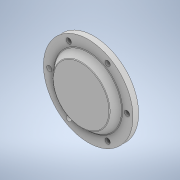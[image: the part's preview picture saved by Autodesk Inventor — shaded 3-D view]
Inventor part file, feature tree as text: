
AUTODESK INVENTOR PART (.ipt)
format: ipt  version: 2020 (Build 240168000, 168)  size: 181,248 bytes
history: native  units: mm
features: sketch x5, reference x4, extrude x3, projected_geometry x3, other x3, plane x2, loft x1, fillet x1
ambient origin geometry x8: Origin, YZ Plane, XZ Plane, XY Plane, X Axis, Y Axis, Z Axis, Center Point
bodies: 实体1 (feature_tree)
feature tree (22):
  plane  "工作平面1"
  extrude  "拉伸1"  Depth=11.0mm
  extrude  "拉伸2"  Depth=12.0mm TaperAngle=0.0deg
  sketch  "草图3"  dims[d8=10.0mm d9=10.5mm d10=0.0mm]
  plane  "工作平面2"
  loft  "放样1"
  extrude  "拉伸3"  Depth=15.0mm
  fillet  "圆角1"  [1 undecoded]
  sketch  "草图1"  dims[d0=165.0mm d1=11.0mm]
  reference  "参考1"
  reference  "参考2"
  reference  "参考3"
  sketch  "草图2"  dims[d2=60.0mm d4=360.0deg d6=12.0mm d7=0.0mm]
  reference  "参考4"
  projected_geometry  "投影回路1"
  sketch  "草图4"  dims[d11=2.0mm d12=15.0mm d13=0.0mm d14=90.0deg]
  projected_geometry  "投影回路2"
  sketch  "草图5"  dims[d15=0.0mm d16=90.0deg d17=5.0mm d18=0.0mm d19=2.0mm]
  projected_geometry  "投影回路3"
  other  "<userpath>\Desktop\ME_course_project\课设试试\shaft_try_1.iam"
  other  "shaft_try_1.iam"
  other  "xia(1):1"
note: 1 required parameter value undecoded (feature->parameter linkage not recoverable at this tier; creation-order binding heuristic only, values carry confidence <= 0.55)
